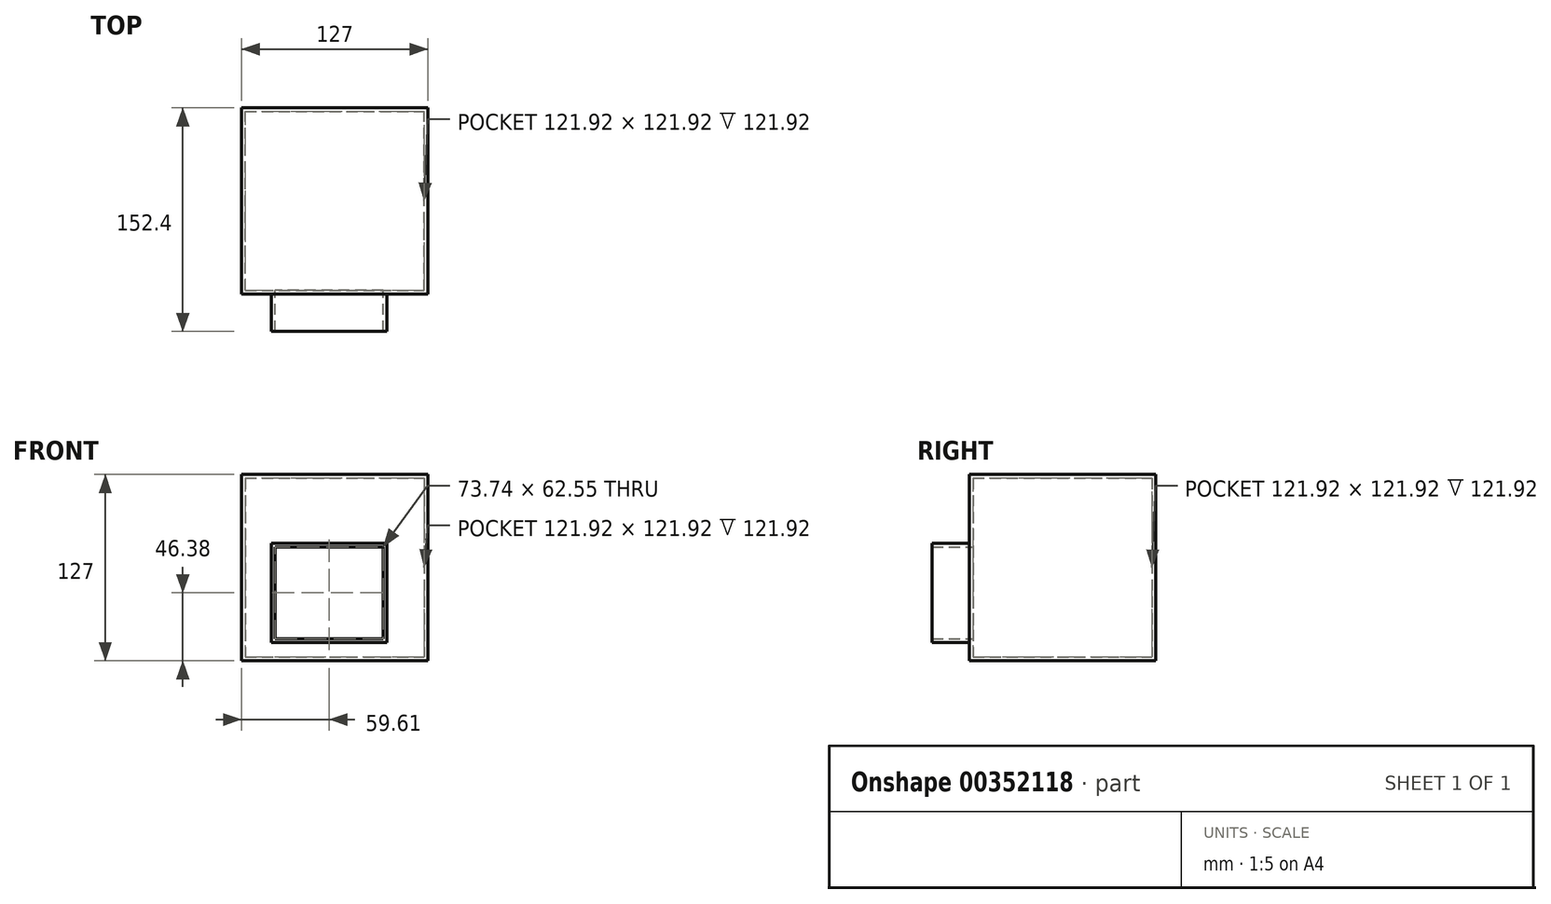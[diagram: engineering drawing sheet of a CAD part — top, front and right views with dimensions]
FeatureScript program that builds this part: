
annotation { "Feature Type Name" : "Feature", "Feature Type Description" : "" }
export const myFeature = defineFeature(function(context is Context, id is Id, definition is map)
    precondition{}
    {
        {
            var Q0;
            Q0=qCreatedBy(makeId("Front.planeOp"),FACE);
            var sketch = newSketch(context, id + "F0", { "sketchPlane" : qUnion([Q0])});
            skLineSegment(sketch, "E0.bottom", {"start": v(-59.61, 80.62) * mm, "end": v(67.39, 80.62) * mm});
            skLineSegment(sketch, "E0.top", {"start": v(-59.61, -46.38) * mm, "end": v(67.39, -46.38) * mm});
            skLineSegment(sketch, "E0.left", {"start": v(-59.61, 80.62) * mm, "end": v(-59.61, -46.38) * mm});
            skLineSegment(sketch, "E0.right", {"start": v(67.39, 80.62) * mm, "end": v(67.39, -46.38) * mm});
            skSolve(sketch);
        }
        {
            var Q0;
            Q0 = qSketchRegion(id + "F0", true);
            extrude(context, id + "F1", {"entities" : qUnion([Q0]), "depth" : 127 * mm});
        }
        {
            var Q0;
            Q0=makeQuery(id+"F1.opExtrude","CAP_FACE",FACE,{"disambiguationData":[OSD([sQuery(id+"F0.wireOp",EDGE,"E0.bottom"),sQuery(id+"F0.wireOp",EDGE,"E0.top"),sQuery(id+"F0.wireOp",EDGE,"E0.left"),sQuery(id+"F0.wireOp",EDGE,"E0.right")])],"isStart":false});
            var sketch = newSketch(context, id + "F2", { "sketchPlane" : qUnion([Q0])});
            skLineSegment(sketch, "E1.bottom", {"start": v(39.4, 33.81) * mm, "end": v(-39.4, 33.81) * mm});
            skLineSegment(sketch, "E1.top", {"start": v(39.4, -33.81) * mm, "end": v(-39.4, -33.81) * mm});
            skLineSegment(sketch, "E1.left", {"start": v(39.4, 33.81) * mm, "end": v(39.4, -33.81) * mm});
            skLineSegment(sketch, "E1.right", {"start": v(-39.4, 33.81) * mm, "end": v(-39.4, -33.81) * mm});
            skPoint(sketch, "E1.middle", {"position": v(0, 0) * mm});
            skSolve(sketch);
        }
        {
            var Q0;
            Q0 = qSketchRegion(id + "F2", true);
            extrude(context, id + "F3", {"entities" : qUnion([Q0]), "operationType" : NewBodyOperationType.ADD, "depth" : 25.4 * mm});
        }
        {
            var Q0;
            Q0=makeQuery(id+"F3.opExtrude","CAP_FACE",FACE,{"disambiguationData":[OSD([sQuery(id+"F2.wireOp",EDGE,"E1.bottom"),sQuery(id+"F2.wireOp",EDGE,"E1.top"),sQuery(id+"F2.wireOp",EDGE,"E1.left"),sQuery(id+"F2.wireOp",EDGE,"E1.right")])],"isStart":false});
            shell(context, id + "F4", {"entities" : qUnion([Q0]), "thickness" : 2.54 * mm});
        }
    });
